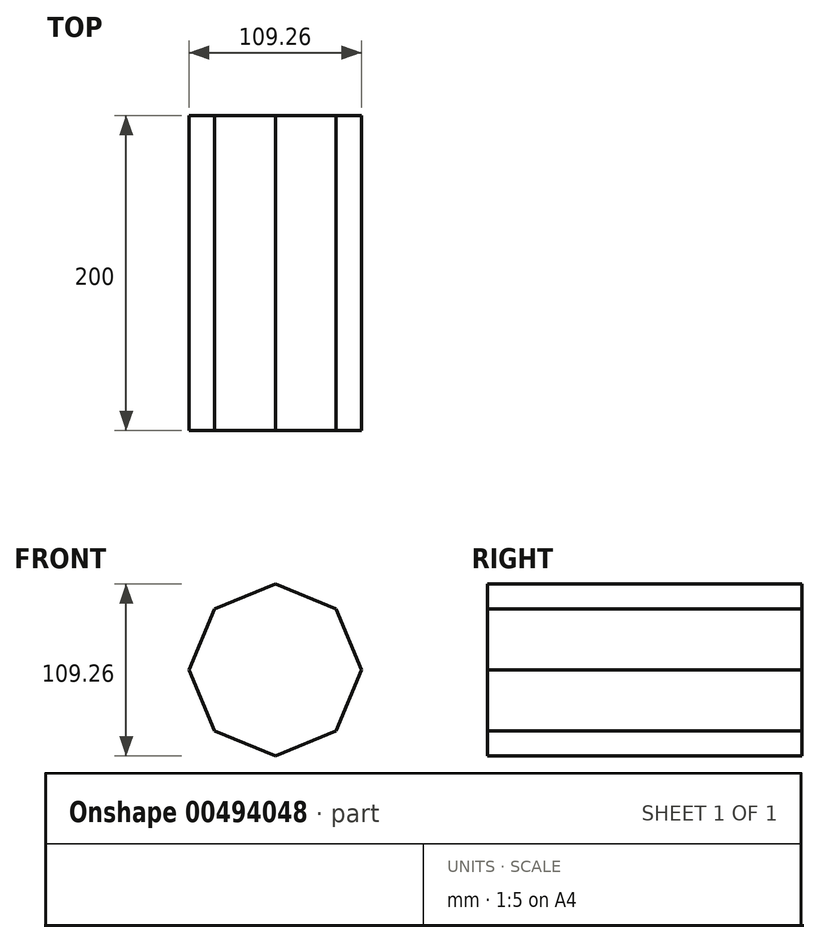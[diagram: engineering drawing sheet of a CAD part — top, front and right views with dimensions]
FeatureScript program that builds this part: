
annotation { "Feature Type Name" : "Feature", "Feature Type Description" : "" }
export const myFeature = defineFeature(function(context is Context, id is Id, definition is map)
    precondition{}
    {
        {
            var Q0;
            Q0=qCreatedBy(makeId("Front.planeOp"),FACE);
            var sketch = newSketch(context, id + "F0", { "sketchPlane" : qUnion([Q0])});
            skCircle(sketch, "E0.cCircle", {"center": v(0, 0) * mm, "radius": 54.63 * mm, "construction": true});
            skLineSegment(sketch, "E0.0", {"start": v(0, 54.63) * mm, "end": v(38.63, 38.63) * mm});
            skLineSegment(sketch, "E0.1", {"start": v(38.63, 38.63) * mm, "end": v(54.63, 0) * mm});
            skLineSegment(sketch, "E0.2", {"start": v(54.63, 0) * mm, "end": v(38.63, -38.63) * mm});
            skLineSegment(sketch, "E0.3", {"start": v(38.63, -38.63) * mm, "end": v(0, -54.63) * mm});
            skLineSegment(sketch, "E0.4", {"start": v(0, -54.63) * mm, "end": v(-38.63, -38.63) * mm});
            skLineSegment(sketch, "E0.5", {"start": v(-38.63, -38.63) * mm, "end": v(-54.63, 0) * mm});
            skLineSegment(sketch, "E0.6", {"start": v(-54.63, 0) * mm, "end": v(-38.63, 38.63) * mm});
            skLineSegment(sketch, "E0.7", {"start": v(-38.63, 38.63) * mm, "end": v(0, 54.63) * mm});
            skSolve(sketch);
        }
        {
            var Q0;
            Q0=makeQuery(id+"F0.imprint","IMPRINT",FACE,{"disambiguationData":[TD([[makeQuery(id+"F0.imprint","IMPRINT",EDGE,{"derivedFrom":sQuery(id+"F0.wireOp",EDGE,"E0.0")}),-1.0]])]});
            extrude(context, id + "F1", {"entities" : qUnion([Q0]), "depth" : 200 * mm});
        }
    });
